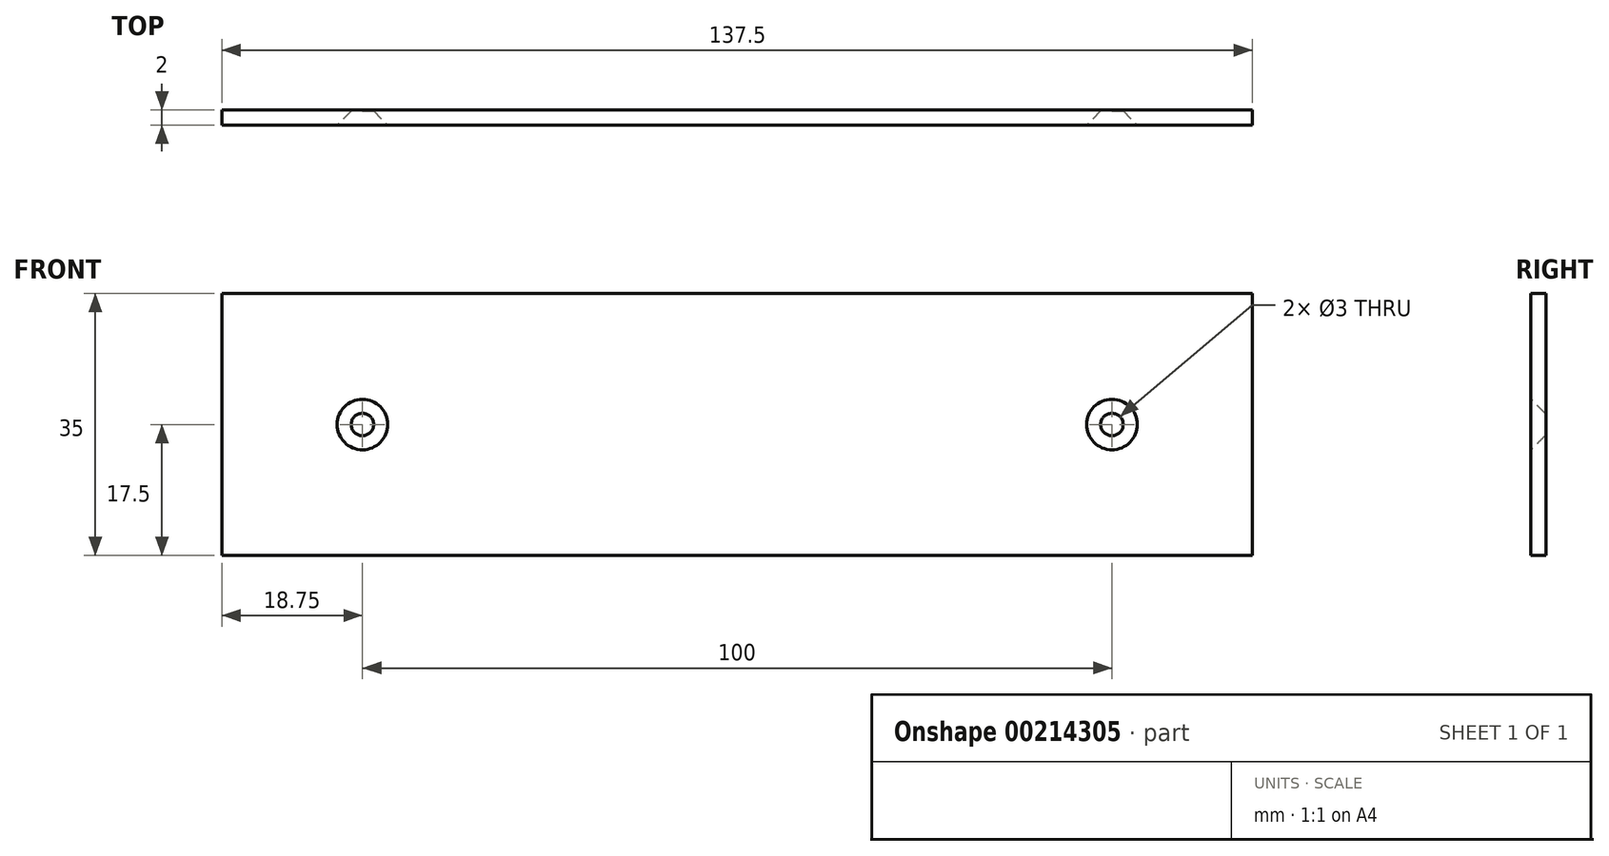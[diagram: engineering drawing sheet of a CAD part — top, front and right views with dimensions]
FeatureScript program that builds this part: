
annotation { "Feature Type Name" : "Feature", "Feature Type Description" : "" }
export const myFeature = defineFeature(function(context is Context, id is Id, definition is map)
    precondition{}
    {
        {
            var Q0;
            Q0=qCreatedBy(makeId("Front.planeOp"),FACE);
            var sketch = newSketch(context, id + "F0", { "sketchPlane" : qUnion([Q0])});
            skLineSegment(sketch, "E0.bottom", {"start": v(68.75, 17.5) * mm, "end": v(-68.75, 17.5) * mm});
            skLineSegment(sketch, "E0.top", {"start": v(68.75, -17.5) * mm, "end": v(-68.75, -17.5) * mm});
            skLineSegment(sketch, "E0.left", {"start": v(68.75, 17.5) * mm, "end": v(68.75, -17.5) * mm});
            skLineSegment(sketch, "E0.right", {"start": v(-68.75, 17.5) * mm, "end": v(-68.75, -17.5) * mm});
            skPoint(sketch, "E0.middle", {"position": v(0, 0) * mm});
            skSolve(sketch);
        }
        {
            var Q0;
            Q0 = qSketchRegion(id + "F0", true);
            extrude(context, id + "F1", {"entities" : qUnion([Q0]), "depth" : 2 * mm});
        }
        {
            var Q0;
            Q0=makeQuery(id+"F1.opExtrude","CAP_FACE",FACE,{"disambiguationData":[OSD([sQuery(id+"F0.wireOp",EDGE,"E0.bottom"),sQuery(id+"F0.wireOp",EDGE,"E0.top"),sQuery(id+"F0.wireOp",EDGE,"E0.left"),sQuery(id+"F0.wireOp",EDGE,"E0.right")])],"isStart":true});
            var sketch = newSketch(context, id + "F2", { "sketchPlane" : qUnion([Q0])});
            skLineSegment(sketch, "E1.bottom", {"start": v(50, 0) * mm, "end": v(-50, 0) * mm, "construction": true});
            skLineSegment(sketch, "E1.top", {"start": v(50, 0) * mm, "end": v(-50, 0) * mm, "construction": true});
            skLineSegment(sketch, "E1.left", {"start": v(50, 0) * mm, "end": v(50, 0) * mm});
            skLineSegment(sketch, "E1.right", {"start": v(-50, 0) * mm, "end": v(-50, 0) * mm});
            skPoint(sketch, "E1.middle", {"position": v(0, 0) * mm});
            skCircle(sketch, "E2", {"center": v(-50, 0) * mm, "radius": 1.5 * mm});
            skCircle(sketch, "E3", {"center": v(50, 0) * mm, "radius": 1.5 * mm});
            skSolve(sketch);
        }
        {
            var Q0;
            Q0 = qSketchRegion(id + "F2", true);
            extrude(context, id + "F3", {"entities" : qUnion([Q0]), "operationType" : NewBodyOperationType.REMOVE, "oppositeDirection" : true, "depth" : 25 * mm});
        }
        {
            var Q0;
            Q0=makeQuery(id+"F3.boolean.opBoolean","INTERSECT",EDGE,{"derivedFrom":[makeQuery(id+"F1.opExtrude","CAP_FACE",FACE,{"disambiguationData":[OSD([sQuery(id+"F0.wireOp",EDGE,"E0.bottom"),sQuery(id+"F0.wireOp",EDGE,"E0.top"),sQuery(id+"F0.wireOp",EDGE,"E0.left"),sQuery(id+"F0.wireOp",EDGE,"E0.right")])],"isStart":false}),makeQuery(id+"F3.opExtrude","SWEPT_FACE",FACE,{"disambiguationData":[OSD([sQuery(id+"F2.wireOp",EDGE,"E2")])]})]});
            var Q1;
            Q1=makeQuery(id+"F3.boolean.opBoolean","INTERSECT",EDGE,{"derivedFrom":[makeQuery(id+"F1.opExtrude","CAP_FACE",FACE,{"disambiguationData":[OSD([sQuery(id+"F0.wireOp",EDGE,"E0.bottom"),sQuery(id+"F0.wireOp",EDGE,"E0.top"),sQuery(id+"F0.wireOp",EDGE,"E0.left"),sQuery(id+"F0.wireOp",EDGE,"E0.right")])],"isStart":false}),makeQuery(id+"F3.opExtrude","SWEPT_FACE",FACE,{"disambiguationData":[OSD([sQuery(id+"F2.wireOp",EDGE,"E3")])]})]});
            chamfer(context, id + "F4", {"entities" : qUnion([Q0, Q1]), "width" : 1.87 * mm, "tangentPropagation" : true});
        }
    });
